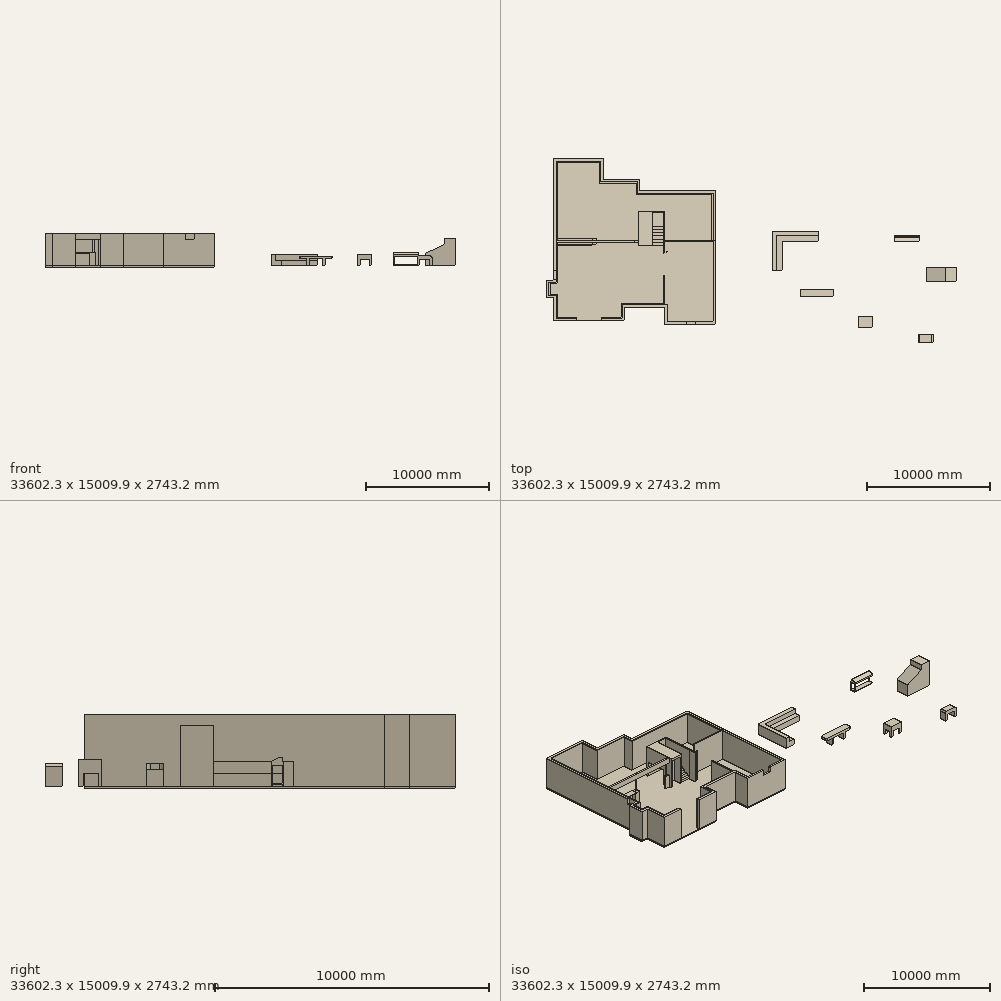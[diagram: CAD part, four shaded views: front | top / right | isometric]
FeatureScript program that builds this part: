
annotation { "Feature Type Name" : "Feature", "Feature Type Description" : "" }
export const myFeature = defineFeature(function(context is Context, id is Id, definition is map)
    precondition{}
    {
        {
            var Q0;
            Q0=qCreatedBy(makeId("Top.planeOp"),FACE);
            var sketch = newSketch(context, id + "F0", { "sketchPlane" : qUnion([Q0])});
            skLineSegment(sketch, "E0", {"start": v(-127, 1524) * mm, "end": v(6096, 1524) * mm});
            skLineSegment(sketch, "E1", {"start": v(6096, 1524) * mm, "end": v(6096, -9042.4) * mm});
            skLineSegment(sketch, "E2", {"start": v(-127, 1524) * mm, "end": v(-127, 2438.4) * mm});
            skLineSegment(sketch, "E3", {"start": v(-127, 2438.4) * mm, "end": v(-3124.2, 2438.4) * mm});
            skLineSegment(sketch, "E4", {"start": v(-3124.2, 2438.4) * mm, "end": v(-3124.2, 4114.8) * mm});
            skLineSegment(sketch, "E5", {"start": v(-3124.2, 4114.8) * mm, "end": v(-6756.4, 4114.8) * mm});
            skLineSegment(sketch, "E6", {"start": v(-6756.4, 4114.8) * mm, "end": v(-6756.4, -5816.6) * mm});
            skLineSegment(sketch, "E7", {"start": v(-6756.4, -5816.6) * mm, "end": v(-7366, -5816.6) * mm});
            skLineSegment(sketch, "E8", {"start": v(-7366, -5816.6) * mm, "end": v(-7366, -6858) * mm});
            skLineSegment(sketch, "E9", {"start": v(-7366, -6858) * mm, "end": v(-6756.4, -6858) * mm});
            skLineSegment(sketch, "E10", {"start": v(-6756.4, -6858) * mm, "end": v(-6756.4, -8737.6) * mm});
            skLineSegment(sketch, "E11", {"start": v(-6756.4, -8737.6) * mm, "end": v(-5080, -8737.6) * mm});
            skLineSegment(sketch, "E12", {"start": v(-5080, -8737.6) * mm, "end": v(-5080, -8890) * mm});
            skLineSegment(sketch, "E13", {"start": v(-3048, -8890) * mm, "end": v(-3048, -8737.6) * mm});
            skLineSegment(sketch, "E14", {"start": v(-3048, -8737.6) * mm, "end": v(-1346.2, -8737.6) * mm});
            skLineSegment(sketch, "E15", {"start": v(-1346.2, -8737.6) * mm, "end": v(-1346.2, -7620) * mm});
            skLineSegment(sketch, "E16", {"start": v(-1346.2, -7620) * mm, "end": v(2311.4, -7620) * mm});
            skLineSegment(sketch, "E17", {"start": v(2311.4, -7620) * mm, "end": v(2311.4, -9042.4) * mm});
            skLineSegment(sketch, "E18", {"start": v(2311.4, -9042.4) * mm, "end": v(6096, -9042.4) * mm});
            skLineSegment(sketch, "E19.bottom", {"start": v(0, 0) * mm, "end": v(2133.6, 0) * mm});
            skLineSegment(sketch, "E19.top", {"start": v(0, -2794) * mm, "end": v(2133.6, -2794) * mm});
            skLineSegment(sketch, "E19.left", {"start": v(0, 0) * mm, "end": v(0, -2794) * mm});
            skLineSegment(sketch, "E19.right", {"start": v(2133.6, 0) * mm, "end": v(2133.6, -2794) * mm});
            skLineSegment(sketch, "E20", {"start": v(2133.6, -2438.4) * mm, "end": v(6096, -2438.4) * mm, "construction": true});
            skLineSegment(sketch, "E21.0", {"start": v(-6959.6, 4318) * mm, "end": v(-6959.6, -5613.4) * mm});
            skLineSegment(sketch, "E21.1", {"start": v(-2921, 4318) * mm, "end": v(-6959.6, 4318) * mm});
            skLineSegment(sketch, "E21.2", {"start": v(76.2, 1727.2) * mm, "end": v(6299.2, 1727.2) * mm});
            skLineSegment(sketch, "E21.3", {"start": v(76.2, 1727.2) * mm, "end": v(76.2, 2641.6) * mm});
            skLineSegment(sketch, "E21.4", {"start": v(76.2, 2641.6) * mm, "end": v(-2921, 2641.6) * mm});
            skLineSegment(sketch, "E21.5", {"start": v(-2921, 2641.6) * mm, "end": v(-2921, 4318) * mm});
            skLineSegment(sketch, "E22.0", {"start": v(-6959.6, -8940.8) * mm, "end": v(-5080, -8940.8) * mm});
            skLineSegment(sketch, "E22.1", {"start": v(-6959.6, -5613.4) * mm, "end": v(-7569.2, -5613.4) * mm});
            skLineSegment(sketch, "E22.2", {"start": v(-7569.2, -5613.4) * mm, "end": v(-7569.2, -7061.2) * mm});
            skLineSegment(sketch, "E22.3", {"start": v(-7569.2, -7061.2) * mm, "end": v(-6959.6, -7061.2) * mm});
            skLineSegment(sketch, "E22.4", {"start": v(-6959.6, -7061.2) * mm, "end": v(-6959.6, -8940.8) * mm});
            skLineSegment(sketch, "E23.0", {"start": v(-3048, -8940.8) * mm, "end": v(-1143, -8940.8) * mm});
            skLineSegment(sketch, "E23.1", {"start": v(-1143, -8940.8) * mm, "end": v(-1143, -7823.2) * mm});
            skLineSegment(sketch, "E23.2", {"start": v(6299.2, 1727.2) * mm, "end": v(6299.2, -9245.6) * mm});
            skLineSegment(sketch, "E23.3", {"start": v(2108.2, -9245.6) * mm, "end": v(6299.2, -9245.6) * mm});
            skLineSegment(sketch, "E23.4", {"start": v(2108.2, -7823.2) * mm, "end": v(2108.2, -9245.6) * mm});
            skLineSegment(sketch, "E23.5", {"start": v(-1143, -7823.2) * mm, "end": v(2108.2, -7823.2) * mm});
            skLineSegment(sketch, "E24", {"start": v(-5080, -8940.8) * mm, "end": v(-5080, -8890) * mm});
            skLineSegment(sketch, "E25", {"start": v(-3048, -8940.8) * mm, "end": v(-3048, -8890) * mm});
            skSolve(sketch);
        }
        {
            var Q0;
            Q0=qCreatedBy(makeId("Top.planeOp"),FACE);
            var sketch = newSketch(context, id + "F1", { "sketchPlane" : qUnion([Q0])});
            skCircle(sketch, "E26", {"center": v(-279.4, -2438.4) * mm, "radius": 50.8 * mm});
            skCircle(sketch, "E27", {"center": v(-3632.2, -2438.4) * mm, "radius": 50.8 * mm});
            skCircle(sketch, "E28", {"center": v(2311.4, -3327.4) * mm, "radius": 50.8 * mm});
            skLineSegment(sketch, "E29", {"start": v(-279.4, -2438.4) * mm, "end": v(-3632.2, -2438.4) * mm, "construction": true});
            skSolve(sketch);
        }
        {
            var Q0;
            Q0 = qSketchRegion(id + "F0", true);
            extrude(context, id + "F2", {"entities" : qUnion([Q0]), "depth" : 2641.6 * mm, "offsetDistance" : 25.4 * mm});
        }
        {
            var Q0;
            Q0 = qSketchRegion(id + "F1", true);
            extrude(context, id + "F3", {"entities" : qUnion([Q0]), "depth" : 2641.6 * mm, "offsetDistance" : 25.4 * mm});
        }
        {
            var Q0;
            Q0=qCreatedBy(makeId("Top.planeOp"),FACE);
            var sketch = newSketch(context, id + "F4", { "sketchPlane" : qUnion([Q0])});
            skLineSegment(sketch, "E30", {"start": v(2136.14, -2436.63) * mm, "end": v(6098.54, -2436.63) * mm, "construction": true});
            skLineSegment(sketch, "E31.0", {"start": v(-6957.06, 4319.77) * mm, "end": v(-6957.06, -5611.63) * mm});
            skLineSegment(sketch, "E31.1", {"start": v(-2918.46, 4319.77) * mm, "end": v(-6957.06, 4319.77) * mm});
            skLineSegment(sketch, "E31.2", {"start": v(78.74, 1728.97) * mm, "end": v(6301.74, 1728.97) * mm});
            skLineSegment(sketch, "E31.3", {"start": v(78.74, 1728.97) * mm, "end": v(78.74, 2643.37) * mm});
            skLineSegment(sketch, "E31.4", {"start": v(78.74, 2643.37) * mm, "end": v(-2918.46, 2643.37) * mm});
            skLineSegment(sketch, "E31.5", {"start": v(-2918.46, 2643.37) * mm, "end": v(-2918.46, 4319.77) * mm});
            skLineSegment(sketch, "E32.0", {"start": v(-6957.06, -8939.03) * mm, "end": v(-5077.46, -8939.03) * mm});
            skLineSegment(sketch, "E32.1", {"start": v(-6957.06, -5611.63) * mm, "end": v(-7566.66, -5611.63) * mm});
            skLineSegment(sketch, "E32.2", {"start": v(-7566.66, -5611.63) * mm, "end": v(-7566.66, -7059.43) * mm});
            skLineSegment(sketch, "E32.3", {"start": v(-7566.66, -7059.43) * mm, "end": v(-6957.06, -7059.43) * mm});
            skLineSegment(sketch, "E32.4", {"start": v(-6957.06, -7059.43) * mm, "end": v(-6957.06, -8939.03) * mm});
            skLineSegment(sketch, "E33.0", {"start": v(-3045.46, -8939.03) * mm, "end": v(-1140.46, -8939.03) * mm});
            skLineSegment(sketch, "E33.1", {"start": v(-1140.46, -8939.03) * mm, "end": v(-1140.46, -7821.43) * mm});
            skLineSegment(sketch, "E33.2", {"start": v(6301.74, 1728.97) * mm, "end": v(6301.74, -9243.83) * mm});
            skLineSegment(sketch, "E33.3", {"start": v(2110.74, -9243.83) * mm, "end": v(6301.74, -9243.83) * mm});
            skLineSegment(sketch, "E33.4", {"start": v(2110.74, -7821.43) * mm, "end": v(2110.74, -9243.83) * mm});
            skLineSegment(sketch, "E33.5", {"start": v(-1140.46, -7821.43) * mm, "end": v(2110.74, -7821.43) * mm});
            skLineSegment(sketch, "E34", {"start": v(-5077.46, -8939.03) * mm, "end": v(-3045.46, -8939.03) * mm});
            skSolve(sketch);
        }
        {
            var Q0;
            Q0 = qSketchRegion(id + "F4", true);
            extrude(context, id + "F5", {"entities" : qUnion([Q0]), "oppositeDirection" : true, "depth" : 101.6 * mm, "offsetDistance" : 25.4 * mm});
        }
        {
            var Q0;
            Q0=makeQuery(id+"F2.opExtrude","CAP_FACE",FACE,{"disambiguationData":[OSD([sQuery(id+"F0.wireOp",EDGE,"E0"),sQuery(id+"F0.wireOp",EDGE,"E1"),sQuery(id+"F0.wireOp",EDGE,"E2"),sQuery(id+"F0.wireOp",EDGE,"E3"),sQuery(id+"F0.wireOp",EDGE,"E4"),sQuery(id+"F0.wireOp",EDGE,"E5"),sQuery(id+"F0.wireOp",EDGE,"E6"),sQuery(id+"F0.wireOp",EDGE,"E7"),sQuery(id+"F0.wireOp",EDGE,"E8"),sQuery(id+"F0.wireOp",EDGE,"E9"),sQuery(id+"F0.wireOp",EDGE,"E10"),sQuery(id+"F0.wireOp",EDGE,"E11"),sQuery(id+"F0.wireOp",EDGE,"E12"),sQuery(id+"F0.wireOp",EDGE,"E13"),sQuery(id+"F0.wireOp",EDGE,"E14"),sQuery(id+"F0.wireOp",EDGE,"E15"),sQuery(id+"F0.wireOp",EDGE,"E16"),sQuery(id+"F0.wireOp",EDGE,"E17"),sQuery(id+"F0.wireOp",EDGE,"E18"),sQuery(id+"F0.wireOp",EDGE,"E21.0"),sQuery(id+"F0.wireOp",EDGE,"E21.1"),sQuery(id+"F0.wireOp",EDGE,"E21.2"),sQuery(id+"F0.wireOp",EDGE,"E21.3"),sQuery(id+"F0.wireOp",EDGE,"E21.4"),sQuery(id+"F0.wireOp",EDGE,"E21.5"),sQuery(id+"F0.wireOp",EDGE,"E22.0"),sQuery(id+"F0.wireOp",EDGE,"E22.1"),sQuery(id+"F0.wireOp",EDGE,"E22.2"),sQuery(id+"F0.wireOp",EDGE,"E22.3"),sQuery(id+"F0.wireOp",EDGE,"E22.4"),sQuery(id+"F0.wireOp",EDGE,"E23.0"),sQuery(id+"F0.wireOp",EDGE,"E23.1"),sQuery(id+"F0.wireOp",EDGE,"E23.2"),sQuery(id+"F0.wireOp",EDGE,"E23.3"),sQuery(id+"F0.wireOp",EDGE,"E23.4"),sQuery(id+"F0.wireOp",EDGE,"E23.5"),sQuery(id+"F0.wireOp",EDGE,"E24"),sQuery(id+"F0.wireOp",EDGE,"E25")])],"isStart":false});
            var sketch = newSketch(context, id + "F6", { "sketchPlane" : qUnion([Q0])});
            skLineSegment(sketch, "E35", {"start": v(-6959.6, -5588) * mm, "end": v(-6756.4, -5588) * mm});
            skLineSegment(sketch, "E36", {"start": v(-6756.4, -5588) * mm, "end": v(-6756.4, -4826) * mm});
            skLineSegment(sketch, "E37", {"start": v(-6756.4, -4826) * mm, "end": v(-6959.6, -4826) * mm});
            skLineSegment(sketch, "E38", {"start": v(-6959.6, -4826) * mm, "end": v(-6959.6, -5588) * mm});
            skLineSegment(sketch, "E39.bottom", {"start": v(3886.2, -9245.6) * mm, "end": v(4648.2, -9245.6) * mm});
            skLineSegment(sketch, "E39.top", {"start": v(3886.2, -9042.4) * mm, "end": v(4648.2, -9042.4) * mm});
            skLineSegment(sketch, "E39.left", {"start": v(3886.2, -9245.6) * mm, "end": v(3886.2, -9042.4) * mm});
            skLineSegment(sketch, "E39.right", {"start": v(4648.2, -9245.6) * mm, "end": v(4648.2, -9042.4) * mm});
            skSolve(sketch);
        }
        {
            var Q0;
            Q0 = qSketchRegion(id + "F6", true);
            extrude(context, id + "F7", {"entities" : qUnion([Q0]), "operationType" : NewBodyOperationType.REMOVE, "oppositeDirection" : true, "depth" : 457.2 * mm, "offsetDistance" : 25.4 * mm});
        }
        {
            var Q0;
            Q0=makeQuery(id+"F2.opExtrude","SWEPT_FACE",FACE,{"disambiguationData":[OSD([sQuery(id+"F0.wireOp",EDGE,"E19.top")])]});
            var sketch = newSketch(context, id + "F8", { "sketchPlane" : qUnion([Q0])});
            skLineSegment(sketch, "E40.bottom", {"start": v(1117.6, 0) * mm, "end": v(2032, 0) * mm});
            skLineSegment(sketch, "E40.top", {"start": v(1117.6, 2641.6) * mm, "end": v(2032, 2641.6) * mm});
            skLineSegment(sketch, "E40.left", {"start": v(1117.6, 0) * mm, "end": v(1117.6, 2641.6) * mm});
            skLineSegment(sketch, "E40.right", {"start": v(2032, 0) * mm, "end": v(2032, 2641.6) * mm});
            skSolve(sketch);
        }
        {
            var Q0;
            Q0=makeQuery(id+"F8.imprint","IMPRINT",FACE,{"disambiguationData":[TD([[makeQuery(id+"F8.imprint","IMPRINT",EDGE,{"derivedFrom":sQuery(id+"F8.wireOp",EDGE,"E40.bottom")}),1.0]])]});
            extrude(context, id + "F9", {"entities" : qUnion([Q0]), "operationType" : NewBodyOperationType.REMOVE, "oppositeDirection" : true, "depth" : 2692.4 * mm, "offsetDistance" : 25.4 * mm});
        }
        {
            var Q0;
            Q0=makeQuery(id+"F2.opExtrude","SWEPT_FACE",FACE,{"disambiguationData":[OSD([sQuery(id+"F0.wireOp",EDGE,"E19.right")])]});
            var sketch = newSketch(context, id + "F10", { "sketchPlane" : qUnion([Q0])});
            skLineSegment(sketch, "E41", {"start": v(-2755.4, 0) * mm, "end": v(-2755.4, 203.2) * mm});
            skLineSegment(sketch, "E42", {"start": v(-2755.4, 203.2) * mm, "end": v(-2501.4, 203.2) * mm});
            skLineSegment(sketch, "E43", {"start": v(-2501.4, 203.2) * mm, "end": v(-2501.4, 406.4) * mm});
            skLineSegment(sketch, "E44", {"start": v(-2501.4, 406.4) * mm, "end": v(-2247.4, 406.4) * mm});
            skLineSegment(sketch, "E45", {"start": v(-2247.4, 406.4) * mm, "end": v(-2247.4, 609.6) * mm});
            skLineSegment(sketch, "E46", {"start": v(-2247.4, 609.6) * mm, "end": v(-1993.4, 609.6) * mm});
            skLineSegment(sketch, "E47", {"start": v(-1993.4, 609.6) * mm, "end": v(-1993.4, 812.8) * mm});
            skLineSegment(sketch, "E48", {"start": v(-1993.4, 812.8) * mm, "end": v(-1739.4, 812.8) * mm});
            skLineSegment(sketch, "E49", {"start": v(-1739.4, 812.8) * mm, "end": v(-1739.4, 1016) * mm});
            skLineSegment(sketch, "E50", {"start": v(-1739.4, 1016) * mm, "end": v(-1485.4, 1016) * mm});
            skLineSegment(sketch, "E51", {"start": v(0, 1121.03) * mm, "end": v(0, 0) * mm});
            skLineSegment(sketch, "E52", {"start": v(0, 0) * mm, "end": v(-2755.4, 0) * mm});
            skLineSegment(sketch, "E53", {"start": v(-1485.4, 1016) * mm, "end": v(-1485.4, 1219.2) * mm});
            skLineSegment(sketch, "E54", {"start": v(-1485.4, 1219.2) * mm, "end": v(-1231.4, 1219.2) * mm});
            skLineSegment(sketch, "E55", {"start": v(-1231.4, 1219.2) * mm, "end": v(-1231.4, 1422.4) * mm});
            skLineSegment(sketch, "E56", {"start": v(-1231.4, 1422.4) * mm, "end": v(0, 1422.4) * mm});
            skLineSegment(sketch, "E57", {"start": v(0, 1422.4) * mm, "end": v(0, 1121.03) * mm});
            skSolve(sketch);
        }
        {
            var Q0;
            Q0=makeQuery(id+"F10.imprint","IMPRINT",FACE,{"disambiguationData":[TD([[makeQuery(id+"F10.imprint","IMPRINT",EDGE,{"derivedFrom":sQuery(id+"F10.wireOp",EDGE,"E41")}),-1.0]])]});
            extrude(context, id + "F11", {"entities" : qUnion([Q0]), "operationType" : NewBodyOperationType.ADD, "oppositeDirection" : true, "depth" : 1016 * mm, "offsetDistance" : 25.4 * mm});
        }
        {
            var Q0;
            Q0=makeQuery(id+"F5.opExtrude","CAP_FACE",FACE,{"disambiguationData":[OSD([sQuery(id+"F4.wireOp",EDGE,"E31.0"),sQuery(id+"F4.wireOp",EDGE,"E31.1"),sQuery(id+"F4.wireOp",EDGE,"E31.2"),sQuery(id+"F4.wireOp",EDGE,"E31.3"),sQuery(id+"F4.wireOp",EDGE,"E31.4"),sQuery(id+"F4.wireOp",EDGE,"E31.5"),sQuery(id+"F4.wireOp",EDGE,"E32.0"),sQuery(id+"F4.wireOp",EDGE,"E32.1"),sQuery(id+"F4.wireOp",EDGE,"E32.2"),sQuery(id+"F4.wireOp",EDGE,"E32.3"),sQuery(id+"F4.wireOp",EDGE,"E32.4"),sQuery(id+"F4.wireOp",EDGE,"E33.0"),sQuery(id+"F4.wireOp",EDGE,"E33.1"),sQuery(id+"F4.wireOp",EDGE,"E33.2"),sQuery(id+"F4.wireOp",EDGE,"E33.3"),sQuery(id+"F4.wireOp",EDGE,"E33.4"),sQuery(id+"F4.wireOp",EDGE,"E33.5"),sQuery(id+"F4.wireOp",EDGE,"E34")])],"isStart":true});
            var sketch = newSketch(context, id + "F12", { "sketchPlane" : qUnion([Q0])});
            skLineSegment(sketch, "E58.bottom", {"start": v(2133.6, -2438.4) * mm, "end": v(6197.6, -2438.4) * mm});
            skLineSegment(sketch, "E58.top", {"start": v(2133.6, -2336.8) * mm, "end": v(6197.6, -2336.8) * mm});
            skLineSegment(sketch, "E58.left", {"start": v(2133.6, -2438.4) * mm, "end": v(2133.6, -2336.8) * mm});
            skLineSegment(sketch, "E58.right", {"start": v(6197.6, -2438.4) * mm, "end": v(6197.6, -2336.8) * mm});
            skSolve(sketch);
        }
        {
            var Q0;
            Q0 = qSketchRegion(id + "F12", true);
            extrude(context, id + "F13", {"entities" : qUnion([Q0]), "depth" : 2641.6 * mm, "offsetDistance" : 25.4 * mm});
        }
        {
            var Q0;
            Q0=makeQuery(id+"F5.opExtrude","CAP_FACE",FACE,{"disambiguationData":[OSD([sQuery(id+"F4.wireOp",EDGE,"E31.0"),sQuery(id+"F4.wireOp",EDGE,"E31.1"),sQuery(id+"F4.wireOp",EDGE,"E31.2"),sQuery(id+"F4.wireOp",EDGE,"E31.3"),sQuery(id+"F4.wireOp",EDGE,"E31.4"),sQuery(id+"F4.wireOp",EDGE,"E31.5"),sQuery(id+"F4.wireOp",EDGE,"E32.0"),sQuery(id+"F4.wireOp",EDGE,"E32.1"),sQuery(id+"F4.wireOp",EDGE,"E32.2"),sQuery(id+"F4.wireOp",EDGE,"E32.3"),sQuery(id+"F4.wireOp",EDGE,"E32.4"),sQuery(id+"F4.wireOp",EDGE,"E33.0"),sQuery(id+"F4.wireOp",EDGE,"E33.1"),sQuery(id+"F4.wireOp",EDGE,"E33.2"),sQuery(id+"F4.wireOp",EDGE,"E33.3"),sQuery(id+"F4.wireOp",EDGE,"E33.4"),sQuery(id+"F4.wireOp",EDGE,"E33.5"),sQuery(id+"F4.wireOp",EDGE,"E34")])],"isStart":true});
            var sketch = newSketch(context, id + "F14", { "sketchPlane" : qUnion([Q0])});
            skLineSegment(sketch, "E59.bottom", {"start": v(2032, -2794) * mm, "end": v(2133.6, -2794) * mm});
            skLineSegment(sketch, "E59.top", {"start": v(2032, -3403.6) * mm, "end": v(2133.6, -3403.6) * mm});
            skLineSegment(sketch, "E59.left", {"start": v(2032, -2794) * mm, "end": v(2032, -3403.6) * mm});
            skLineSegment(sketch, "E59.right", {"start": v(2133.6, -2794) * mm, "end": v(2133.6, -3403.6) * mm});
            skLineSegment(sketch, "E60", {"start": v(2133.6, -3403.6) * mm, "end": v(2133.6, -5232.4) * mm, "construction": true});
            skLineSegment(sketch, "E61.bottom", {"start": v(2133.6, -5232.4) * mm, "end": v(2032, -5232.4) * mm});
            skLineSegment(sketch, "E61.top", {"start": v(2133.6, -7649.03) * mm, "end": v(2032, -7649.03) * mm});
            skLineSegment(sketch, "E61.left", {"start": v(2133.6, -5232.4) * mm, "end": v(2133.6, -7649.03) * mm});
            skLineSegment(sketch, "E61.right", {"start": v(2032, -5232.4) * mm, "end": v(2032, -7649.03) * mm});
            skSolve(sketch);
        }
        {
            var Q0;
            Q0 = qSketchRegion(id + "F14", true);
            extrude(context, id + "F15", {"entities" : qUnion([Q0]), "depth" : 2641.6 * mm, "offsetDistance" : 25.4 * mm});
        }
        {
            var Q0;
            Q0=makeQuery(id+"F5.opExtrude","CAP_FACE",FACE,{"disambiguationData":[OSD([sQuery(id+"F4.wireOp",EDGE,"E31.0"),sQuery(id+"F4.wireOp",EDGE,"E31.1"),sQuery(id+"F4.wireOp",EDGE,"E31.2"),sQuery(id+"F4.wireOp",EDGE,"E31.3"),sQuery(id+"F4.wireOp",EDGE,"E31.4"),sQuery(id+"F4.wireOp",EDGE,"E31.5"),sQuery(id+"F4.wireOp",EDGE,"E32.0"),sQuery(id+"F4.wireOp",EDGE,"E32.1"),sQuery(id+"F4.wireOp",EDGE,"E32.2"),sQuery(id+"F4.wireOp",EDGE,"E32.3"),sQuery(id+"F4.wireOp",EDGE,"E32.4"),sQuery(id+"F4.wireOp",EDGE,"E33.0"),sQuery(id+"F4.wireOp",EDGE,"E33.1"),sQuery(id+"F4.wireOp",EDGE,"E33.2"),sQuery(id+"F4.wireOp",EDGE,"E33.3"),sQuery(id+"F4.wireOp",EDGE,"E33.4"),sQuery(id+"F4.wireOp",EDGE,"E33.5"),sQuery(id+"F4.wireOp",EDGE,"E34")])],"isStart":true});
            var sketch = newSketch(context, id + "F16", { "sketchPlane" : qUnion([Q0])});
            skLineSegment(sketch, "E62.bottom", {"start": v(-6654.8, -2667) * mm, "end": v(-3479.8, -2667) * mm});
            skLineSegment(sketch, "E62.top", {"start": v(-6654.8, -2209.8) * mm, "end": v(-3479.8, -2209.8) * mm});
            skLineSegment(sketch, "E62.left", {"start": v(-6654.8, -2667) * mm, "end": v(-6654.8, -2209.8) * mm});
            skLineSegment(sketch, "E62.right", {"start": v(-3479.8, -2667) * mm, "end": v(-3479.8, -2209.8) * mm});
            skLineSegment(sketch, "E63.bottom", {"start": v(0, -2540) * mm, "end": v(-406.4, -2540) * mm});
            skLineSegment(sketch, "E63.top", {"start": v(0, -2349.5) * mm, "end": v(-406.4, -2349.5) * mm});
            skLineSegment(sketch, "E63.left", {"start": v(0, -2540) * mm, "end": v(0, -2349.5) * mm});
            skLineSegment(sketch, "E63.right", {"start": v(-406.4, -2540) * mm, "end": v(-406.4, -2349.5) * mm});
            skSolve(sketch);
        }
        {
            var Q0;
            Q0 = qSketchRegion(id + "F16", true);
            extrude(context, id + "F17", {"entities" : qUnion([Q0]), "depth" : 1066.8 * mm, "offsetDistance" : 25.4 * mm});
        }
        {
            var Q0;
            {var subQ0=sQuery(id+"F0.wireOp",EDGE,"E18");var subQ1=sQuery(id+"F0.wireOp",EDGE,"E6");var subQ2=sQuery(id+"F0.wireOp",EDGE,"E21.4");var subQ3=sQuery(id+"F0.wireOp",EDGE,"E5");var subQ4=sQuery(id+"F0.wireOp",EDGE,"E21.3");var subQ5=sQuery(id+"F0.wireOp",EDGE,"E21.1");var subQ6=sQuery(id+"F0.wireOp",EDGE,"E3");var subQ7=sQuery(id+"F0.wireOp",EDGE,"E4");var subQ8=sQuery(id+"F0.wireOp",EDGE,"E21.2");var subQ9=sQuery(id+"F0.wireOp",EDGE,"E0");var subQ10=sQuery(id+"F0.wireOp",EDGE,"E21.0");var subQ11=sQuery(id+"F0.wireOp",EDGE,"E2");var subQ12=sQuery(id+"F0.wireOp",EDGE,"E1");var subQ13=sQuery(id+"F0.wireOp",EDGE,"E21.5");var subQ14=sQuery(id+"F0.wireOp",EDGE,"E23.2");var subQ15=sQuery(id+"F0.wireOp",EDGE,"E23.3");Q0=makeQuery(id+"F7.boolean.opBoolean","SPLIT",FACE,{"disambiguationData":[TD([makeQuery(id+"F2.opExtrude","SWEPT_FACE",FACE,{"disambiguationData":[OSD([subQ9])]})])],"derivedFrom":makeQuery(id+"F2.opExtrude","CAP_FACE",FACE,{"disambiguationData":[OSD([subQ9,subQ12,subQ11,subQ6,subQ7,subQ3,subQ1,sQuery(id+"F0.wireOp",EDGE,"E7"),sQuery(id+"F0.wireOp",EDGE,"E8"),sQuery(id+"F0.wireOp",EDGE,"E9"),sQuery(id+"F0.wireOp",EDGE,"E10"),sQuery(id+"F0.wireOp",EDGE,"E11"),sQuery(id+"F0.wireOp",EDGE,"E12"),sQuery(id+"F0.wireOp",EDGE,"E13"),sQuery(id+"F0.wireOp",EDGE,"E14"),sQuery(id+"F0.wireOp",EDGE,"E15"),sQuery(id+"F0.wireOp",EDGE,"E16"),sQuery(id+"F0.wireOp",EDGE,"E17"),subQ0,subQ10,subQ5,subQ8,subQ4,subQ2,subQ13,sQuery(id+"F0.wireOp",EDGE,"E22.0"),sQuery(id+"F0.wireOp",EDGE,"E22.1"),sQuery(id+"F0.wireOp",EDGE,"E22.2"),sQuery(id+"F0.wireOp",EDGE,"E22.3"),sQuery(id+"F0.wireOp",EDGE,"E22.4"),sQuery(id+"F0.wireOp",EDGE,"E23.0"),sQuery(id+"F0.wireOp",EDGE,"E23.1"),subQ14,subQ15,sQuery(id+"F0.wireOp",EDGE,"E23.4"),sQuery(id+"F0.wireOp",EDGE,"E23.5"),sQuery(id+"F0.wireOp",EDGE,"E24"),sQuery(id+"F0.wireOp",EDGE,"E25")])],"isStart":false})});}
            var sketch = newSketch(context, id + "F18", { "sketchPlane" : qUnion([Q0])});
            skLineSegment(sketch, "E64.bottom", {"start": v(0, -2349.5) * mm, "end": v(-6756.4, -2349.5) * mm});
            skLineSegment(sketch, "E64.top", {"start": v(0, -2540.11) * mm, "end": v(-6756.4, -2540.11) * mm});
            skLineSegment(sketch, "E64.left", {"start": v(0, -2349.5) * mm, "end": v(0, -2540.11) * mm});
            skLineSegment(sketch, "E64.right", {"start": v(-6756.4, -2349.5) * mm, "end": v(-6756.4, -2540.11) * mm});
            skSolve(sketch);
        }
        {
            var Q0;
            Q0 = qSketchRegion(id + "F18", true);
            extrude(context, id + "F19", {"entities" : qUnion([Q0]), "oppositeDirection" : true, "depth" : 457.2 * mm, "offsetDistance" : 25.4 * mm});
        }
        {
            var Q0;
            Q0=makeQuery(id+"F5.opExtrude","CAP_FACE",FACE,{"disambiguationData":[OSD([sQuery(id+"F4.wireOp",EDGE,"E31.0"),sQuery(id+"F4.wireOp",EDGE,"E31.1"),sQuery(id+"F4.wireOp",EDGE,"E31.2"),sQuery(id+"F4.wireOp",EDGE,"E31.3"),sQuery(id+"F4.wireOp",EDGE,"E31.4"),sQuery(id+"F4.wireOp",EDGE,"E31.5"),sQuery(id+"F4.wireOp",EDGE,"E32.0"),sQuery(id+"F4.wireOp",EDGE,"E32.1"),sQuery(id+"F4.wireOp",EDGE,"E32.2"),sQuery(id+"F4.wireOp",EDGE,"E32.3"),sQuery(id+"F4.wireOp",EDGE,"E32.4"),sQuery(id+"F4.wireOp",EDGE,"E33.0"),sQuery(id+"F4.wireOp",EDGE,"E33.1"),sQuery(id+"F4.wireOp",EDGE,"E33.2"),sQuery(id+"F4.wireOp",EDGE,"E33.3"),sQuery(id+"F4.wireOp",EDGE,"E33.4"),sQuery(id+"F4.wireOp",EDGE,"E33.5"),sQuery(id+"F4.wireOp",EDGE,"E34")])],"isStart":true});
            var sketch = newSketch(context, id + "F20", { "sketchPlane" : qUnion([Q0])});
            skLineSegment(sketch, "E65.0", {"start": v(-6654.8, -8636) * mm, "end": v(-5080, -8636) * mm});
            skLineSegment(sketch, "E65.1", {"start": v(-6654.8, -6756.4) * mm, "end": v(-6654.8, -8636) * mm});
            skLineSegment(sketch, "E65.2", {"start": v(-228.6, 2336.8) * mm, "end": v(-3225.8, 2336.8) * mm});
            skLineSegment(sketch, "E65.3", {"start": v(-228.6, 1422.4) * mm, "end": v(-228.6, 2336.8) * mm});
            skLineSegment(sketch, "E65.4", {"start": v(-228.6, 1422.4) * mm, "end": v(5994.4, 1422.4) * mm});
            skLineSegment(sketch, "E65.5", {"start": v(5994.4, 1422.4) * mm, "end": v(5994.4, -2379.6) * mm});
            skLineSegment(sketch, "E65.6", {"start": v(-3225.8, 2336.8) * mm, "end": v(-3225.8, 4013.2) * mm});
            skLineSegment(sketch, "E65.7", {"start": v(-3225.8, 4013.2) * mm, "end": v(-6654.8, 4013.2) * mm});
            skLineSegment(sketch, "E65.8", {"start": v(-6654.8, 4013.2) * mm, "end": v(-6654.8, -5918.2) * mm});
            skLineSegment(sketch, "E65.9", {"start": v(-6654.8, -5918.2) * mm, "end": v(-7264.4, -5918.2) * mm});
            skLineSegment(sketch, "E65.10", {"start": v(-7264.4, -5918.2) * mm, "end": v(-7264.4, -6756.4) * mm});
            skLineSegment(sketch, "E65.11", {"start": v(-7264.4, -6756.4) * mm, "end": v(-6654.8, -6756.4) * mm});
            skPoint(sketch, "E66", {"position": v(5994.4, -2379.6) * mm});
            skLineSegment(sketch, "E67", {"start": v(5994.4, -2379.6) * mm, "end": v(6096, -2379.6) * mm});
            skLineSegment(sketch, "E68.0.0", {"start": v(4648.2, -9042.4) * mm, "end": v(4648.2, -9245.6) * mm});
            skLineSegment(sketch, "E68.0.1", {"start": v(4648.2, -9245.6) * mm, "end": v(6299.2, -9245.6) * mm});
            skLineSegment(sketch, "E68.0.10", {"start": v(-6756.4, -4826) * mm, "end": v(-6756.4, 4114.8) * mm});
            skLineSegment(sketch, "E68.0.11", {"start": v(-6756.4, 4114.8) * mm, "end": v(-3124.2, 4114.8) * mm});
            skLineSegment(sketch, "E68.0.12", {"start": v(-3124.2, 4114.8) * mm, "end": v(-3124.2, 2438.4) * mm});
            skLineSegment(sketch, "E68.0.13", {"start": v(-3124.2, 2438.4) * mm, "end": v(-127, 2438.4) * mm});
            skLineSegment(sketch, "E68.0.14", {"start": v(-127, 2438.4) * mm, "end": v(-127, 1524) * mm});
            skLineSegment(sketch, "E68.0.15", {"start": v(-127, 1524) * mm, "end": v(6096, 1524) * mm});
            skLineSegment(sketch, "E68.0.16", {"start": v(6096, 1524) * mm, "end": v(6096, -2379.6) * mm});
            skLineSegment(sketch, "E68.0.17", {"start": v(6096, -9042.4) * mm, "end": v(4648.2, -9042.4) * mm});
            skPoint(sketch, "E69.orphan", {"position": v(6096, -9042.4) * mm});
            skPoint(sketch, "E68.0.3.end.orphan", {"position": v(76.2, 1727.2) * mm});
            skPoint(sketch, "E68.0.2.end.orphan", {"position": v(6299.2, 1727.2) * mm});
            skPoint(sketch, "E68.0.5.start.orphan", {"position": v(76.2, 2641.6) * mm});
            skPoint(sketch, "E68.0.6.start.orphan", {"position": v(-2921, 2641.6) * mm});
            skPoint(sketch, "E68.0.7.start.orphan", {"position": v(-2921, 4318) * mm});
            skPoint(sketch, "E68.0.8.start.orphan", {"position": v(-6959.6, 4318) * mm});
            skPoint(sketch, "E68.0.9.start.orphan", {"position": v(-6959.6, -4826) * mm});
            skLineSegment(sketch, "E70.0", {"start": v(-6756.4, -8737.6) * mm, "end": v(-5080, -8737.6) * mm});
            skLineSegment(sketch, "E71.0", {"start": v(-6756.4, -6858) * mm, "end": v(-6756.4, -8737.6) * mm});
            skLineSegment(sketch, "E72.0", {"start": v(-7366, -6858) * mm, "end": v(-6756.4, -6858) * mm});
            skLineSegment(sketch, "E73.0", {"start": v(-7366, -5816.6) * mm, "end": v(-7366, -6858) * mm});
            skLineSegment(sketch, "E74.0", {"start": v(-6756.4, -5816.6) * mm, "end": v(-7366, -5816.6) * mm});
            skLineSegment(sketch, "E75", {"start": v(-5080, -8737.6) * mm, "end": v(-5080, -8636) * mm});
            skLineSegment(sketch, "E76", {"start": v(-6756.4, -5816.6) * mm, "end": v(-6756.4, -4826) * mm});
            skLineSegment(sketch, "E77.0", {"start": v(-1447.8, -7518.4) * mm, "end": v(2102.79, -7518.4) * mm});
            skLineSegment(sketch, "E77.1", {"start": v(-1447.8, -8636) * mm, "end": v(-1447.8, -7518.4) * mm});
            skLineSegment(sketch, "E77.2", {"start": v(-3048, -8636) * mm, "end": v(-1447.8, -8636) * mm});
            skLineSegment(sketch, "E78.0", {"start": v(-3048, -8737.6) * mm, "end": v(-1346.2, -8737.6) * mm});
            skLineSegment(sketch, "E79.0", {"start": v(-1346.2, -8737.6) * mm, "end": v(-1346.2, -7620) * mm});
            skLineSegment(sketch, "E80.0", {"start": v(-1346.2, -7620) * mm, "end": v(2102.79, -7620) * mm});
            skLineSegment(sketch, "E81", {"start": v(-3048, -8737.6) * mm, "end": v(-3048, -8636) * mm});
            skLineSegment(sketch, "E82", {"start": v(2102.79, -7620) * mm, "end": v(2102.79, -7518.4) * mm});
            skPoint(sketch, "E83.orphan", {"position": v(2311.4, -7620) * mm});
            skSolve(sketch);
        }
        {
            var Q0;
            Q0=makeQuery(id+"F20.imprint","IMPRINT",FACE,{"disambiguationData":[TD([[makeQuery(id+"F20.imprint","IMPRINT",EDGE,{"derivedFrom":sQuery(id+"F20.wireOp",EDGE,"E65.0")}),-1.0]])]});
            var Q1;
            Q1=makeQuery(id+"F20.imprint","IMPRINT",FACE,{"disambiguationData":[TD([[makeQuery(id+"F20.imprint","IMPRINT",EDGE,{"derivedFrom":sQuery(id+"F20.wireOp",EDGE,"E77.0")}),-1.0]])]});
            extrude(context, id + "F21", {"entities" : qUnion([Q0, Q1]), "depth" : 2641.6 * mm, "offsetDistance" : 25.4 * mm});
        }
        {
            var Q0;
            {var subQ1=sQuery(id+"F0.wireOp",EDGE,"E19.left");var subQ2=sQuery(id+"F0.wireOp",EDGE,"E19.top");Q0=makeQuery(id+"F9.boolean.opBoolean","SPLIT",FACE,{"disambiguationData":[TD([makeQuery(id+"F2.opExtrude","SWEPT_FACE",FACE,{"disambiguationData":[OSD([subQ1])]})])],"derivedFrom":makeQuery(id+"F2.opExtrude","SWEPT_FACE",FACE,{"disambiguationData":[OSD([subQ2])]})});}
            var sketch = newSketch(context, id + "F22", { "sketchPlane" : qUnion([Q0])});
            skLineSegment(sketch, "E84.bottom", {"start": v(76.2, 0) * mm, "end": v(1028.7, 0) * mm});
            skLineSegment(sketch, "E84.top", {"start": v(76.2, 2438.4) * mm, "end": v(1028.7, 2438.4) * mm});
            skLineSegment(sketch, "E84.left", {"start": v(76.2, 0) * mm, "end": v(76.2, 2438.4) * mm});
            skLineSegment(sketch, "E84.right", {"start": v(1028.7, 0) * mm, "end": v(1028.7, 2438.4) * mm});
            skSolve(sketch);
        }
        {
            var Q0;
            Q0=makeQuery(id+"F22.imprint","IMPRINT",FACE,{"disambiguationData":[TD([[makeQuery(id+"F22.imprint","IMPRINT",EDGE,{"derivedFrom":sQuery(id+"F22.wireOp",EDGE,"E84.bottom")}),1.0]])]});
            extrude(context, id + "F23", {"entities" : qUnion([Q0]), "operationType" : NewBodyOperationType.REMOVE, "oppositeDirection" : true, "depth" : 762 * mm, "offsetDistance" : 25.4 * mm});
        }
        {
            var Q0;
            Q0=makeQuery(id+"F2.opExtrude","SWEPT_FACE",FACE,{"disambiguationData":[OSD([sQuery(id+"F0.wireOp",EDGE,"E19.left")])]});
            var sketch = newSketch(context, id + "F24", { "sketchPlane" : qUnion([Q0])});
            skLineSegment(sketch, "E85.bottom", {"start": v(152.4, 0) * mm, "end": v(1930.4, 0) * mm});
            skLineSegment(sketch, "E85.top", {"start": v(152.4, 1270) * mm, "end": v(1930.4, 1270) * mm});
            skLineSegment(sketch, "E85.left", {"start": v(152.4, 0) * mm, "end": v(152.4, 1270) * mm});
            skLineSegment(sketch, "E85.right", {"start": v(1930.4, 0) * mm, "end": v(1930.4, 1270) * mm});
            skSolve(sketch);
        }
        {
            var Q0;
            Q0=makeQuery(id+"F9.boolean.opBoolean","COPY",FACE,{"derivedFrom":makeQuery(id+"F9.opExtrude","SWEPT_FACE",FACE,{"disambiguationData":[OSD([sQuery(id+"F8.wireOp",EDGE,"E40.left")])]})});
            var Q1;
            Q1=makeQuery(id+"F9.boolean.opBoolean","COPY",FACE,{"derivedFrom":makeQuery(id+"F9.opExtrude","SWEPT_FACE",FACE,{"disambiguationData":[OSD([sQuery(id+"F8.wireOp",EDGE,"E40.right")])]})});
            var Q2;
            Q2=makeQuery(id+"F24.imprint","IMPRINT",FACE,{"disambiguationData":[TD([[makeQuery(id+"F24.imprint","IMPRINT",EDGE,{"derivedFrom":sQuery(id+"F24.wireOp",EDGE,"E85.bottom")}),1.0]])]});
            extrude(context, id + "F25", {"entities" : qUnion([Q0, Q1, Q2]), "operationType" : NewBodyOperationType.REMOVE, "depth" : 914.4 * mm, "offsetDistance" : 25.4 * mm});
        }
        {
            var Q0;
            Q0=makeQuery(id+"F25.boolean.opBoolean","COPY",FACE,{"derivedFrom":makeQuery(id+"F25.opExtrude","CAP_FACE",FACE,{"disambiguationData":[OSD([sQuery(id+"F24.wireOp",EDGE,"E85.bottom"),sQuery(id+"F24.wireOp",EDGE,"E85.top"),sQuery(id+"F24.wireOp",EDGE,"E85.left"),sQuery(id+"F24.wireOp",EDGE,"E85.right")])],"isStart":false})});
            var sketch = newSketch(context, id + "F26", { "sketchPlane" : qUnion([Q0])});
            skLineSegment(sketch, "E86.bottom", {"start": v(152.4, 0) * mm, "end": v(1066.8, 0) * mm});
            skLineSegment(sketch, "E86.top", {"start": v(152.4, 1270) * mm, "end": v(1066.8, 1270) * mm});
            skLineSegment(sketch, "E86.left", {"start": v(152.4, 0) * mm, "end": v(152.4, 1270) * mm});
            skLineSegment(sketch, "E86.right", {"start": v(1066.8, 0) * mm, "end": v(1066.8, 1270) * mm});
            skSolve(sketch);
        }
        {
            var Q0;
            Q0=makeQuery(id+"F26.imprint","IMPRINT",FACE,{"disambiguationData":[TD([[makeQuery(id+"F26.imprint","IMPRINT",EDGE,{"derivedFrom":sQuery(id+"F26.wireOp",EDGE,"E86.bottom")}),1.0]])]});
            extrude(context, id + "F27", {"entities" : qUnion([Q0]), "operationType" : NewBodyOperationType.REMOVE, "oppositeDirection" : true, "depth" : 1219.2 * mm, "offsetDistance" : 25.4 * mm});
        }
        {
            var Q0;
            Q0=makeQuery(id+"F16.imprint","IMPRINT",FACE,{"disambiguationData":[TD([[makeQuery(id+"F16.imprint","IMPRINT",EDGE,{"derivedFrom":sQuery(id+"F16.wireOp",EDGE,"E62.bottom")}),-1.0]])]});
            var sketch = newSketch(context, id + "F28", { "sketchPlane" : qUnion([Q0])});
            skSolve(sketch);
        }
        {
            var Q0;
            Q0=makeQuery(id+"F17.opExtrude","SWEPT_FACE",FACE,{"disambiguationData":[OSD([sQuery(id+"F16.wireOp",EDGE,"E62.bottom")])]});
            var sketch = newSketch(context, id + "F29", { "sketchPlane" : qUnion([Q0])});
            skLineSegment(sketch, "E87.bottom", {"start": v(-6502.4, 0) * mm, "end": v(-3937, 0) * mm});
            skLineSegment(sketch, "E87.top", {"start": v(-6502.4, 990.6) * mm, "end": v(-3937, 990.6) * mm});
            skLineSegment(sketch, "E87.left", {"start": v(-6502.4, 0) * mm, "end": v(-6502.4, 990.6) * mm});
            skLineSegment(sketch, "E87.right", {"start": v(-3937, 0) * mm, "end": v(-3937, 990.6) * mm});
            skSolve(sketch);
        }
        {
            var Q0;
            Q0=makeQuery(id+"F29.imprint","IMPRINT",FACE,{"disambiguationData":[TD([[makeQuery(id+"F29.imprint","IMPRINT",EDGE,{"derivedFrom":sQuery(id+"F29.wireOp",EDGE,"E87.bottom")}),1.0]])]});
            extrude(context, id + "F30", {"entities" : qUnion([Q0]), "operationType" : NewBodyOperationType.REMOVE, "oppositeDirection" : true, "depth" : 304.8 * mm, "offsetDistance" : 25.4 * mm});
        }
        {
            var Q0;
            Q0=makeQuery(id+"F2.opExtrude","SWEPT_FACE",FACE,{"disambiguationData":[OSD([sQuery(id+"F0.wireOp",EDGE,"E19.bottom")])]});
            var sketch = newSketch(context, id + "F31", { "sketchPlane" : qUnion([Q0])});
            skLineSegment(sketch, "E88.bottom", {"start": v(-2133.6, 0) * mm, "end": v(-2032, 0) * mm});
            skLineSegment(sketch, "E88.top", {"start": v(-2133.6, 2641.6) * mm, "end": v(-2032, 2641.6) * mm});
            skLineSegment(sketch, "E88.left", {"start": v(-2133.6, 0) * mm, "end": v(-2133.6, 2641.6) * mm});
            skLineSegment(sketch, "E88.right", {"start": v(-2032, 0) * mm, "end": v(-2032, 2641.6) * mm});
            skSolve(sketch);
        }
        {
            var Q0;
            Q0=makeQuery(id+"F31.imprint","IMPRINT",FACE,{"disambiguationData":[TD([[makeQuery(id+"F31.imprint","IMPRINT",EDGE,{"derivedFrom":sQuery(id+"F31.wireOp",EDGE,"E88.bottom")}),-1.0]])]});
            extrude(context, id + "F32", {"entities" : qUnion([Q0]), "oppositeDirection" : true, "depth" : 2794 * mm, "offsetDistance" : 25.4 * mm});
        }
        {
            var Q0;
            Q0=makeQuery(id+"F32.opExtrude","SWEPT_BODY",BODY,{"disambiguationData":[OSD([sQuery(id+"F31.wireOp",EDGE,"E88.bottom"),sQuery(id+"F31.wireOp",EDGE,"E88.top"),sQuery(id+"F31.wireOp",EDGE,"E88.left"),sQuery(id+"F31.wireOp",EDGE,"E88.right")])]});
            var Q1;
            Q1=makeQuery(id+"F2.opExtrude","SWEPT_BODY",BODY,{"disambiguationData":[OSD([sQuery(id+"F0.wireOp",EDGE,"E19.bottom"),sQuery(id+"F0.wireOp",EDGE,"E19.top"),sQuery(id+"F0.wireOp",EDGE,"E19.left"),sQuery(id+"F0.wireOp",EDGE,"E19.right")])]});
            booleanBodies(context, id + "F33", {"operationType" : BooleanOperationType.UNION, "tools" : qUnion([Q0, Q1])});
        }
        {
            var Q0;
            Q0=makeQuery(id+"F17.opExtrude","CAP_FACE",FACE,{"disambiguationData":[OSD([sQuery(id+"F16.wireOp",EDGE,"E62.bottom"),sQuery(id+"F16.wireOp",EDGE,"E62.top"),sQuery(id+"F16.wireOp",EDGE,"E62.left"),sQuery(id+"F16.wireOp",EDGE,"E62.right")])],"isStart":false});
            var sketch = newSketch(context, id + "F34", { "sketchPlane" : qUnion([Q0])});
            skLineSegment(sketch, "E89", {"start": v(-6654.8, -2667) * mm, "end": v(-6654.8, -2743.2) * mm, "construction": true});
            skLineSegment(sketch, "E90.bottom", {"start": v(-6654.8, -2743.2) * mm, "end": v(-3809.82, -2743.2) * mm});
            skLineSegment(sketch, "E90.top", {"start": v(-6654.8, -2209.8) * mm, "end": v(-3809.82, -2209.8) * mm});
            skLineSegment(sketch, "E90.left", {"start": v(-6654.8, -2743.2) * mm, "end": v(-6654.8, -2209.8) * mm});
            skLineSegment(sketch, "E90.right", {"start": v(-3809.82, -2743.2) * mm, "end": v(-3809.82, -2209.8) * mm});
            skSolve(sketch);
        }
        {
            var Q0;
            {var subQ0=sQuery(id+"F34.wireOp",EDGE,"E90.top");Q0=makeQuery(id+"F34.imprint","IMPRINT",FACE,{"disambiguationData":[TD([[makeQuery(id+"F34.imprint","IMPRINT",EDGE,{"derivedFrom":subQ0}),-1.0]])]});}
            var Q1;
            {var subQ0=sQuery(id+"F34.wireOp",EDGE,"E90.bottom");Q1=makeQuery(id+"F34.imprint","IMPRINT",FACE,{"disambiguationData":[TD([[makeQuery(id+"F34.imprint","IMPRINT",EDGE,{"derivedFrom":subQ0}),1.0]])]});}
            extrude(context, id + "F35", {"entities" : qUnion([Q0, Q1]), "depth" : 31.75 * mm, "offsetDistance" : 25.4 * mm});
        }
        {
            var Q0;
            Q0=makeQuery(id+"F35.opExtrude","CAP_EDGE",EDGE,{"disambiguationData":[OSD([sQuery(id+"F34.wireOp",EDGE,"E90.bottom")])],"isStart":false});
            var Q1;
            Q1=makeQuery(id+"F35.opExtrude","CAP_EDGE",EDGE,{"disambiguationData":[OSD([sQuery(id+"F34.wireOp",EDGE,"E90.right")])],"isStart":false});
            var Q2;
            Q2=makeQuery(id+"F35.opExtrude","CAP_EDGE",EDGE,{"disambiguationData":[OSD([sQuery(id+"F34.wireOp",EDGE,"E90.top")])],"isStart":false});
            chamfer(context, id + "F36", {"entities" : qUnion([Q0, Q1, Q2]), "width" : 12.7 * mm, "tangentPropagation" : true});
        }
        {
            var Q0;
            Q0=makeQuery(id+"F33.opBoolean","SPLIT",FACE,{"disambiguationData":[TD([makeQuery(id+"F25.boolean.opBoolean","COPY",FACE,{"derivedFrom":makeQuery(id+"F25.opExtrude","SWEPT_FACE",FACE,{"disambiguationData":[OSD([sQuery(id+"F24.wireOp",EDGE,"E85.top")])]})})])],"derivedFrom":makeQuery(id+"F32.opExtrude","SWEPT_FACE",FACE,{"disambiguationData":[OSD([sQuery(id+"F31.wireOp",EDGE,"E88.right")])]})});
            extrude(context, id + "F37", {"entities" : qUnion([Q0]), "operationType" : NewBodyOperationType.REMOVE, "oppositeDirection" : true, "depth" : 152.4 * mm, "offsetDistance" : 25.4 * mm});
        }
        {
            var Q0;
            Q0=makeQuery(id+"F28.imprint","IMPRINT",FACE,{"disambiguationData":[TD([[makeQuery(id+"F28.imprint","IMPRINT",EDGE,{"derivedFrom":makeQuery(id+"F16.imprint","IMPRINT",EDGE,{"derivedFrom":sQuery(id+"F16.wireOp",EDGE,"E62.bottom")})}),-1.0]])]});
            var sketch = newSketch(context, id + "F38", { "sketchPlane" : qUnion([Q0])});
            skLineSegment(sketch, "E91.bottom", {"start": v(10915.14, -4793.68) * mm, "end": v(11753.34, -4793.68) * mm});
            skLineSegment(sketch, "E91.left", {"start": v(10915.14, -4793.68) * mm, "end": v(10915.14, -1593.28) * mm});
            skLineSegment(sketch, "E91.right", {"start": v(11753.34, -4793.68) * mm, "end": v(11753.34, -2431.48) * mm});
            skLineSegment(sketch, "E92.bottom", {"start": v(10915.14, -1593.28) * mm, "end": v(14725.14, -1593.28) * mm});
            skLineSegment(sketch, "E92.top", {"start": v(11753.34, -2431.48) * mm, "end": v(14725.14, -2431.48) * mm});
            skLineSegment(sketch, "E92.right", {"start": v(14725.14, -1593.28) * mm, "end": v(14725.14, -2431.48) * mm});
            skSolve(sketch);
        }
        {
            var Q0;
            Q0=makeQuery(id+"F38.imprint","IMPRINT",FACE,{"disambiguationData":[TD([[makeQuery(id+"F38.imprint","IMPRINT",EDGE,{"derivedFrom":sQuery(id+"F38.wireOp",EDGE,"E91.bottom")}),1.0]])]});
            extrude(context, id + "F39", {"entities" : qUnion([Q0]), "depth" : 914.4 * mm, "offsetDistance" : 25.4 * mm});
        }
        {
            var Q0;
            Q0=makeQuery(id+"F39.opExtrude","CAP_FACE",FACE,{"disambiguationData":[OSD([sQuery(id+"F38.wireOp",EDGE,"E91.bottom"),sQuery(id+"F38.wireOp",EDGE,"E91.left"),sQuery(id+"F38.wireOp",EDGE,"E91.right"),sQuery(id+"F38.wireOp",EDGE,"E92.bottom"),sQuery(id+"F38.wireOp",EDGE,"E92.top"),sQuery(id+"F38.wireOp",EDGE,"E92.right")])],"isStart":false});
            var sketch = newSketch(context, id + "F40", { "sketchPlane" : qUnion([Q0])});
            skLineSegment(sketch, "E93", {"start": v(11296.14, -4793.68) * mm, "end": v(11296.14, -1974.28) * mm});
            skLineSegment(sketch, "E94", {"start": v(11296.14, -1974.28) * mm, "end": v(14725.14, -1974.28) * mm});
            skLineSegment(sketch, "E95", {"start": v(14725.14, -1974.28) * mm, "end": v(14725.14, -2431.48) * mm});
            skLineSegment(sketch, "E96", {"start": v(14725.14, -2431.48) * mm, "end": v(11753.34, -2431.48) * mm});
            skLineSegment(sketch, "E97", {"start": v(11753.34, -2431.48) * mm, "end": v(11753.34, -4793.68) * mm});
            skLineSegment(sketch, "E98", {"start": v(11753.34, -4793.68) * mm, "end": v(11296.14, -4793.68) * mm});
            skSolve(sketch);
        }
        {
            var Q0;
            Q0=makeQuery(id+"F40.imprint","IMPRINT",FACE,{"disambiguationData":[TD([[makeQuery(id+"F40.imprint","IMPRINT",EDGE,{"derivedFrom":sQuery(id+"F40.wireOp",EDGE,"E93")}),-1.0]])]});
            extrude(context, id + "F41", {"entities" : qUnion([Q0]), "operationType" : NewBodyOperationType.REMOVE, "oppositeDirection" : true, "depth" : 431.8 * mm, "offsetDistance" : 25.4 * mm});
        }
        {
            var Q0;
            Q0=makeQuery(id+"F28.imprint","IMPRINT",FACE,{"disambiguationData":[TD([[makeQuery(id+"F28.imprint","IMPRINT",EDGE,{"derivedFrom":makeQuery(id+"F16.imprint","IMPRINT",EDGE,{"derivedFrom":sQuery(id+"F16.wireOp",EDGE,"E62.bottom")})}),-1.0]])]});
            var sketch = newSketch(context, id + "F42", { "sketchPlane" : qUnion([Q0])});
            skLineSegment(sketch, "E99.bottom", {"start": v(13229.39, -6380.77) * mm, "end": v(15972.59, -6380.77) * mm});
            skLineSegment(sketch, "E99.top", {"start": v(13229.39, -6990.37) * mm, "end": v(15972.59, -6990.37) * mm});
            skLineSegment(sketch, "E99.left", {"start": v(13229.39, -6380.77) * mm, "end": v(13229.39, -6990.37) * mm});
            skLineSegment(sketch, "E99.right", {"start": v(15972.59, -6380.77) * mm, "end": v(15972.59, -6990.37) * mm});
            skSolve(sketch);
        }
        {
            var Q0;
            Q0=makeQuery(id+"F42.imprint","IMPRINT",FACE,{"disambiguationData":[TD([[makeQuery(id+"F42.imprint","IMPRINT",EDGE,{"derivedFrom":sQuery(id+"F42.wireOp",EDGE,"E99.bottom")}),-1.0]])]});
            extrude(context, id + "F43", {"entities" : qUnion([Q0]), "depth" : 812.8 * mm, "offsetDistance" : 25.4 * mm});
        }
        {
            var Q0;
            Q0=makeQuery(id+"F43.opExtrude","SWEPT_FACE",FACE,{"disambiguationData":[OSD([sQuery(id+"F42.wireOp",EDGE,"E99.top")])]});
            var sketch = newSketch(context, id + "F44", { "sketchPlane" : qUnion([Q0])});
            skLineSegment(sketch, "E100.bottom", {"start": v(13229.39, 0) * mm, "end": v(13838.99, 0) * mm});
            skLineSegment(sketch, "E100.top", {"start": v(13229.39, 609.6) * mm, "end": v(13838.99, 609.6) * mm});
            skLineSegment(sketch, "E100.left", {"start": v(13229.39, 0) * mm, "end": v(13229.39, 609.6) * mm});
            skLineSegment(sketch, "E100.right", {"start": v(13838.99, 0) * mm, "end": v(13838.99, 609.6) * mm});
            skLineSegment(sketch, "E101.bottom", {"start": v(15972.59, 0) * mm, "end": v(15362.99, 0) * mm});
            skLineSegment(sketch, "E101.top", {"start": v(15972.59, 609.6) * mm, "end": v(15362.99, 609.6) * mm});
            skLineSegment(sketch, "E101.left", {"start": v(15972.59, 0) * mm, "end": v(15972.59, 609.6) * mm});
            skLineSegment(sketch, "E101.right", {"start": v(15362.99, 0) * mm, "end": v(15362.99, 609.6) * mm});
            skLineSegment(sketch, "E102.bottom", {"start": v(14042.19, 0) * mm, "end": v(15159.79, 0) * mm});
            skLineSegment(sketch, "E102.top", {"start": v(14042.19, 609.6) * mm, "end": v(15159.79, 609.6) * mm});
            skLineSegment(sketch, "E102.left", {"start": v(14042.19, 0) * mm, "end": v(14042.19, 609.6) * mm});
            skLineSegment(sketch, "E102.right", {"start": v(15159.79, 0) * mm, "end": v(15159.79, 609.6) * mm});
            skSolve(sketch);
        }
        {
            var Q0;
            Q0=makeQuery(id+"F44.imprint","IMPRINT",FACE,{"disambiguationData":[TD([[makeQuery(id+"F44.imprint","IMPRINT",EDGE,{"derivedFrom":sQuery(id+"F44.wireOp",EDGE,"E100.bottom")}),1.0]])]});
            var Q1;
            Q1=makeQuery(id+"F44.imprint","IMPRINT",FACE,{"disambiguationData":[TD([[makeQuery(id+"F44.imprint","IMPRINT",EDGE,{"derivedFrom":sQuery(id+"F44.wireOp",EDGE,"E102.bottom")}),1.0]])]});
            var Q2;
            Q2=makeQuery(id+"F44.imprint","IMPRINT",FACE,{"disambiguationData":[TD([[makeQuery(id+"F44.imprint","IMPRINT",EDGE,{"derivedFrom":sQuery(id+"F44.wireOp",EDGE,"E101.bottom")}),1.0]])]});
            extrude(context, id + "F45", {"entities" : qUnion([Q0, Q1, Q2]), "operationType" : NewBodyOperationType.REMOVE, "oppositeDirection" : true, "depth" : 609.6 * mm, "offsetDistance" : 25.4 * mm});
        }
        {
            var Q0;
            Q0=makeQuery(id+"F43.opExtrude","SWEPT_EDGE",EDGE,{"disambiguationData":[OSD([sQuery(id+"F42.wireOp",EDGE,"E99.top"),sQuery(id+"F42.wireOp",EDGE,"E99.right")])]});
            var Q1;
            Q1=makeQuery(id+"F43.opExtrude","SWEPT_EDGE",EDGE,{"disambiguationData":[OSD([sQuery(id+"F42.wireOp",EDGE,"E99.top"),sQuery(id+"F42.wireOp",EDGE,"E99.left")])]});
            var Q2;
            Q2=makeQuery(id+"F43.opExtrude","SWEPT_EDGE",EDGE,{"disambiguationData":[OSD([sQuery(id+"F42.wireOp",EDGE,"E99.bottom"),sQuery(id+"F42.wireOp",EDGE,"E99.left")])]});
            var Q3;
            Q3=makeQuery(id+"F43.opExtrude","SWEPT_EDGE",EDGE,{"disambiguationData":[OSD([sQuery(id+"F42.wireOp",EDGE,"E99.bottom"),sQuery(id+"F42.wireOp",EDGE,"E99.right")])]});
            fillet(context, id + "F46", {"entities" : qUnion([Q0, Q1, Q2, Q3]), "radius" : 127 * mm, "tangentPropagation" : true, "allowEdgeOverflow" : false});
        }
        {
            var Q0;
            Q0=makeQuery(id+"F28.imprint","IMPRINT",FACE,{"disambiguationData":[TD([[makeQuery(id+"F28.imprint","IMPRINT",EDGE,{"derivedFrom":makeQuery(id+"F16.imprint","IMPRINT",EDGE,{"derivedFrom":sQuery(id+"F16.wireOp",EDGE,"E62.bottom")})}),-1.0]])]});
            var sketch = newSketch(context, id + "F47", { "sketchPlane" : qUnion([Q0])});
            skLineSegment(sketch, "E103.bottom", {"start": v(21015.99, -1961.27) * mm, "end": v(22997.19, -1961.27) * mm});
            skLineSegment(sketch, "E103.top", {"start": v(21015.99, -2418.47) * mm, "end": v(22997.19, -2418.47) * mm});
            skLineSegment(sketch, "E103.left", {"start": v(21015.99, -1961.27) * mm, "end": v(21015.99, -2418.47) * mm});
            skLineSegment(sketch, "E103.right", {"start": v(22997.19, -1961.27) * mm, "end": v(22997.19, -2418.47) * mm});
            skSolve(sketch);
        }
        {
            var Q0;
            Q0=makeQuery(id+"F47.imprint","IMPRINT",FACE,{"disambiguationData":[TD([[makeQuery(id+"F47.imprint","IMPRINT",EDGE,{"derivedFrom":sQuery(id+"F47.wireOp",EDGE,"E103.bottom")}),-1.0]])]});
            extrude(context, id + "F48", {"entities" : qUnion([Q0]), "depth" : 1066.8 * mm, "offsetDistance" : 25.4 * mm});
        }
        {
            var Q0;
            Q0=makeQuery(id+"F48.opExtrude","SWEPT_FACE",FACE,{"disambiguationData":[OSD([sQuery(id+"F47.wireOp",EDGE,"E103.left")])]});
            extrude(context, id + "F49", {"entities" : qUnion([Q0]), "operationType" : NewBodyOperationType.ADD, "depth" : 25.4 * mm, "offsetDistance" : 25.4 * mm});
        }
        {
            var Q0;
            Q0=makeQuery(id+"F49.opExtrude","CAP_FACE",FACE,{"disambiguationData":[OSD([sQuery(id+"F47.wireOp",EDGE,"E103.left")])],"isStart":false});
            var sketch = newSketch(context, id + "F50", { "sketchPlane" : qUnion([Q0])});
            skLineSegment(sketch, "E104", {"start": v(2080.13, 1066.8) * mm, "end": v(2418.47, 909.03) * mm});
            skLineSegment(sketch, "E105.bottom", {"start": v(1999.37, 774.7) * mm, "end": v(2380.37, 774.7) * mm});
            skLineSegment(sketch, "E105.top", {"start": v(1999.37, 114.3) * mm, "end": v(2380.37, 114.3) * mm});
            skLineSegment(sketch, "E105.left", {"start": v(1999.37, 774.7) * mm, "end": v(1999.37, 114.3) * mm});
            skLineSegment(sketch, "E105.right", {"start": v(2380.37, 774.7) * mm, "end": v(2380.37, 114.3) * mm});
            skLineSegment(sketch, "E106.bottom", {"start": v(1999.37, 76.2) * mm, "end": v(2380.37, 76.2) * mm});
            skLineSegment(sketch, "E106.top", {"start": v(1999.37, 0) * mm, "end": v(2380.37, 0) * mm});
            skLineSegment(sketch, "E106.left", {"start": v(1999.37, 76.2) * mm, "end": v(1999.37, 0) * mm});
            skLineSegment(sketch, "E106.right", {"start": v(2380.37, 76.2) * mm, "end": v(2380.37, 0) * mm});
            skLineSegment(sketch, "E107", {"start": v(2418.47, 909.03) * mm, "end": v(1961.27, 909.03) * mm, "construction": true});
            skLineSegment(sketch, "E108.bottom", {"start": v(1961.27, 909.03) * mm, "end": v(2019.36, 909.03) * mm});
            skLineSegment(sketch, "E108.top", {"start": v(1961.27, 1066.8) * mm, "end": v(2019.36, 1066.8) * mm});
            skLineSegment(sketch, "E108.left", {"start": v(1961.27, 909.03) * mm, "end": v(1961.27, 1066.8) * mm});
            skLineSegment(sketch, "E108.right", {"start": v(2019.36, 909.03) * mm, "end": v(2019.36, 1066.8) * mm});
            skSolve(sketch);
        }
        {
            var Q0;
            {var subQ0=sQuery(id+"F50.wireOp",EDGE,"E104");Q0=makeQuery(id+"F50.imprint","IMPRINT",FACE,{"disambiguationData":[TD([[makeQuery(id+"F50.imprint","IMPRINT",EDGE,{"derivedFrom":subQ0}),1.0]])]});}
            var Q1;
            Q1=makeQuery(id+"F50.imprint","IMPRINT",FACE,{"disambiguationData":[TD([[makeQuery(id+"F50.imprint","IMPRINT",EDGE,{"derivedFrom":sQuery(id+"F50.wireOp",EDGE,"E108.bottom")}),1.0]])]});
            var Q2;
            Q2=makeQuery(id+"F50.imprint","IMPRINT",FACE,{"disambiguationData":[TD([[makeQuery(id+"F50.imprint","IMPRINT",EDGE,{"derivedFrom":sQuery(id+"F50.wireOp",EDGE,"E105.bottom")}),-1.0]])]});
            var Q3;
            Q3=makeQuery(id+"F50.imprint","IMPRINT",FACE,{"disambiguationData":[TD([[makeQuery(id+"F50.imprint","IMPRINT",EDGE,{"derivedFrom":sQuery(id+"F50.wireOp",EDGE,"E106.bottom")}),-1.0]])]});
            extrude(context, id + "F51", {"entities" : qUnion([Q0, Q1, Q2, Q3]), "operationType" : NewBodyOperationType.REMOVE, "endBound" : BoundingType.THROUGH_ALL, "oppositeDirection" : true, "depth" : 25.4 * mm, "offsetDistance" : 25.4 * mm});
        }
        {
            var Q0;
            {var subQ0=sQuery(id+"F47.wireOp",EDGE,"E103.top");Q0=makeQuery(id+"F49.boolean.opBoolean","MERGE",FACE,{"derivedFrom":[makeQuery(id+"F48.opExtrude","SWEPT_FACE",FACE,{"disambiguationData":[OSD([subQ0])]}),makeQuery(id+"F49.opExtrude","SWEPT_FACE",FACE,{"disambiguationData":[OSD([subQ0,sQuery(id+"F47.wireOp",EDGE,"E103.left")])]})]});}
            var sketch = newSketch(context, id + "F52", { "sketchPlane" : qUnion([Q0])});
            skLineSegment(sketch, "E109.bottom", {"start": v(21028.69, 0) * mm, "end": v(22959.09, 0) * mm});
            skLineSegment(sketch, "E109.top", {"start": v(21028.69, 76.2) * mm, "end": v(22959.09, 76.2) * mm});
            skLineSegment(sketch, "E109.left", {"start": v(21028.69, 0) * mm, "end": v(21028.69, 76.2) * mm});
            skLineSegment(sketch, "E109.right", {"start": v(22959.09, 0) * mm, "end": v(22959.09, 76.2) * mm});
            skLineSegment(sketch, "E110.bottom", {"start": v(21028.69, 114.3) * mm, "end": v(22959.09, 114.3) * mm});
            skLineSegment(sketch, "E110.top", {"start": v(21028.69, 774.7) * mm, "end": v(22959.09, 774.7) * mm});
            skLineSegment(sketch, "E110.left", {"start": v(21028.69, 114.3) * mm, "end": v(21028.69, 774.7) * mm});
            skLineSegment(sketch, "E110.right", {"start": v(22959.09, 114.3) * mm, "end": v(22959.09, 774.7) * mm});
            skSolve(sketch);
        }
        {
            var Q0;
            Q0=makeQuery(id+"F52.imprint","IMPRINT",FACE,{"disambiguationData":[TD([[makeQuery(id+"F52.imprint","IMPRINT",EDGE,{"derivedFrom":sQuery(id+"F52.wireOp",EDGE,"E110.bottom")}),1.0]])]});
            var Q1;
            Q1=makeQuery(id+"F52.imprint","IMPRINT",FACE,{"disambiguationData":[TD([[makeQuery(id+"F52.imprint","IMPRINT",EDGE,{"derivedFrom":sQuery(id+"F52.wireOp",EDGE,"E109.bottom")}),1.0]])]});
            extrude(context, id + "F53", {"entities" : qUnion([Q0, Q1]), "operationType" : NewBodyOperationType.REMOVE, "endBound" : BoundingType.THROUGH_ALL, "oppositeDirection" : true, "depth" : 25.4 * mm, "offsetDistance" : 25.4 * mm});
        }
        {
            var Q0;
            Q0=makeQuery(id+"F28.imprint","IMPRINT",FACE,{"disambiguationData":[TD([[makeQuery(id+"F28.imprint","IMPRINT",EDGE,{"derivedFrom":makeQuery(id+"F16.imprint","IMPRINT",EDGE,{"derivedFrom":sQuery(id+"F16.wireOp",EDGE,"E62.bottom")})}),-1.0]])]});
            var sketch = newSketch(context, id + "F54", { "sketchPlane" : qUnion([Q0])});
            skLineSegment(sketch, "E111.bottom", {"start": v(23594.75, -5758.56) * mm, "end": v(26033.15, -5758.56) * mm});
            skLineSegment(sketch, "E111.top", {"start": v(23594.75, -4539.36) * mm, "end": v(26033.15, -4539.36) * mm});
            skLineSegment(sketch, "E111.left", {"start": v(23594.75, -5758.56) * mm, "end": v(23594.75, -4539.36) * mm});
            skLineSegment(sketch, "E111.right", {"start": v(26033.15, -5758.56) * mm, "end": v(26033.15, -4539.36) * mm});
            skSolve(sketch);
        }
        {
            var Q0;
            Q0=makeQuery(id+"F54.imprint","IMPRINT",FACE,{"disambiguationData":[TD([[makeQuery(id+"F54.imprint","IMPRINT",EDGE,{"derivedFrom":sQuery(id+"F54.wireOp",EDGE,"E111.bottom")}),1.0]])]});
            extrude(context, id + "F55", {"entities" : qUnion([Q0]), "depth" : 2235.2 * mm, "offsetDistance" : 25.4 * mm});
        }
        {
            var Q0;
            Q0=makeQuery(id+"F55.opExtrude","SWEPT_FACE",FACE,{"disambiguationData":[OSD([sQuery(id+"F54.wireOp",EDGE,"E111.bottom")])]});
            var sketch = newSketch(context, id + "F56", { "sketchPlane" : qUnion([Q0])});
            skLineSegment(sketch, "E112", {"start": v(23594.75, 1016) * mm, "end": v(25118.75, 1770.96) * mm});
            skLineSegment(sketch, "E113", {"start": v(25118.75, 1770.96) * mm, "end": v(25118.75, 2235.2) * mm});
            skSolve(sketch);
        }
        {
            var Q0;
            Q0 = qSketchRegion(id + "F56", true);
            var Q1;
            {var subQ0=sQuery(id+"F56.wireOp",EDGE,"E112");Q1=makeQuery(id+"F56.imprint","IMPRINT",FACE,{"disambiguationData":[TD([[makeQuery(id+"F56.imprint","IMPRINT",EDGE,{"derivedFrom":subQ0}),1.0]])]});}
            extrude(context, id + "F57", {"entities" : qUnion([Q0, Q1]), "operationType" : NewBodyOperationType.REMOVE, "endBound" : BoundingType.THROUGH_ALL, "oppositeDirection" : true, "depth" : 25.4 * mm, "offsetDistance" : 25.4 * mm});
        }
        {
            var Q0;
            Q0=makeQuery(id+"F28.imprint","IMPRINT",FACE,{"disambiguationData":[TD([[makeQuery(id+"F28.imprint","IMPRINT",EDGE,{"derivedFrom":makeQuery(id+"F16.imprint","IMPRINT",EDGE,{"derivedFrom":sQuery(id+"F16.wireOp",EDGE,"E62.bottom")})}),-1.0]])]});
            var sketch = newSketch(context, id + "F58", { "sketchPlane" : qUnion([Q0])});
            skLineSegment(sketch, "E114.bottom", {"start": v(18028.59, -9466.35) * mm, "end": v(19171.59, -9466.35) * mm});
            skLineSegment(sketch, "E114.top", {"start": v(18028.59, -8628.15) * mm, "end": v(19171.59, -8628.15) * mm});
            skLineSegment(sketch, "E114.left", {"start": v(18028.59, -9466.35) * mm, "end": v(18028.59, -8628.15) * mm});
            skLineSegment(sketch, "E114.right", {"start": v(19171.59, -9466.35) * mm, "end": v(19171.59, -8628.15) * mm});
            skSolve(sketch);
        }
        {
            var Q0;
            Q0=makeQuery(id+"F58.imprint","IMPRINT",FACE,{"disambiguationData":[TD([[makeQuery(id+"F58.imprint","IMPRINT",EDGE,{"derivedFrom":sQuery(id+"F58.wireOp",EDGE,"E114.bottom")}),1.0]])]});
            extrude(context, id + "F59", {"entities" : qUnion([Q0]), "depth" : 965.2 * mm, "offsetDistance" : 25.4 * mm});
        }
        {
            var Q0;
            Q0=makeQuery(id+"F28.imprint","IMPRINT",FACE,{"disambiguationData":[TD([[makeQuery(id+"F28.imprint","IMPRINT",EDGE,{"derivedFrom":makeQuery(id+"F16.imprint","IMPRINT",EDGE,{"derivedFrom":sQuery(id+"F16.wireOp",EDGE,"E62.bottom")})}),-1.0]])]});
            var sketch = newSketch(context, id + "F60", { "sketchPlane" : qUnion([Q0])});
            skLineSegment(sketch, "E115.bottom", {"start": v(22903.18, -10690.11) * mm, "end": v(24122.38, -10690.11) * mm});
            skLineSegment(sketch, "E115.top", {"start": v(22903.18, -10080.51) * mm, "end": v(24122.38, -10080.51) * mm});
            skLineSegment(sketch, "E115.left", {"start": v(22903.18, -10690.11) * mm, "end": v(22903.18, -10080.51) * mm});
            skLineSegment(sketch, "E115.right", {"start": v(24122.38, -10690.11) * mm, "end": v(24122.38, -10080.51) * mm});
            skSolve(sketch);
        }
        {
            var Q0;
            Q0=makeQuery(id+"F60.imprint","IMPRINT",FACE,{"disambiguationData":[TD([[makeQuery(id+"F60.imprint","IMPRINT",EDGE,{"derivedFrom":sQuery(id+"F60.wireOp",EDGE,"E115.bottom")}),1.0]])]});
            extrude(context, id + "F61", {"entities" : qUnion([Q0]), "depth" : 838.2 * mm, "offsetDistance" : 25.4 * mm});
        }
        {
            var Q0;
            Q0=makeQuery(id+"F61.opExtrude","CAP_EDGE",EDGE,{"disambiguationData":[OSD([sQuery(id+"F60.wireOp",EDGE,"E115.left")])],"isStart":false});
            var Q1;
            Q1=makeQuery(id+"F61.opExtrude","CAP_EDGE",EDGE,{"disambiguationData":[OSD([sQuery(id+"F60.wireOp",EDGE,"E115.right")])],"isStart":false});
            chamfer(context, id + "F62", {"entities" : qUnion([Q0, Q1]), "width" : 127 * mm, "tangentPropagation" : true});
        }
        {
            var Q0;
            Q0=makeQuery(id+"F61.opExtrude","SWEPT_FACE",FACE,{"disambiguationData":[OSD([sQuery(id+"F60.wireOp",EDGE,"E115.bottom")])]});
            var sketch = newSketch(context, id + "F63", { "sketchPlane" : qUnion([Q0])});
            skLineSegment(sketch, "E116.bottom", {"start": v(23072.4, 0) * mm, "end": v(23941.22, 0) * mm});
            skLineSegment(sketch, "E116.top", {"start": v(23072.4, 535.8) * mm, "end": v(23941.22, 535.8) * mm});
            skLineSegment(sketch, "E116.left", {"start": v(23072.4, 0) * mm, "end": v(23072.4, 535.8) * mm});
            skLineSegment(sketch, "E116.right", {"start": v(23941.22, 0) * mm, "end": v(23941.22, 535.8) * mm});
            skSolve(sketch);
        }
        {
            var Q0;
            Q0 = qSketchRegion(id + "F63", true);
            var Q1;
            Q1=makeQuery(id+"F63.imprint","IMPRINT",FACE,{"disambiguationData":[TD([[makeQuery(id+"F63.imprint","IMPRINT",EDGE,{"derivedFrom":sQuery(id+"F63.wireOp",EDGE,"E116.bottom")}),1.0]])]});
            extrude(context, id + "F64", {"entities" : qUnion([Q0, Q1]), "operationType" : NewBodyOperationType.REMOVE, "oppositeDirection" : true, "depth" : 609.6 * mm, "offsetDistance" : 25.4 * mm});
        }
        {
            var Q0;
            Q0=makeQuery(id+"F59.opExtrude","SWEPT_FACE",FACE,{"disambiguationData":[OSD([sQuery(id+"F58.wireOp",EDGE,"E114.bottom")])]});
            var sketch = newSketch(context, id + "F65", { "sketchPlane" : qUnion([Q0])});
            skLineSegment(sketch, "E117.bottom", {"start": v(18260.11, 0) * mm, "end": v(18948.95, 0) * mm});
            skLineSegment(sketch, "E117.top", {"start": v(18260.11, 509.38) * mm, "end": v(18948.95, 509.38) * mm});
            skLineSegment(sketch, "E117.left", {"start": v(18260.11, 0) * mm, "end": v(18260.11, 509.38) * mm});
            skLineSegment(sketch, "E117.right", {"start": v(18948.95, 0) * mm, "end": v(18948.95, 509.38) * mm});
            skSolve(sketch);
        }
        {
            var Q0;
            Q0=makeQuery(id+"F65.imprint","IMPRINT",FACE,{"disambiguationData":[TD([[makeQuery(id+"F65.imprint","IMPRINT",EDGE,{"derivedFrom":sQuery(id+"F65.wireOp",EDGE,"E117.bottom")}),1.0]])]});
            extrude(context, id + "F66", {"entities" : qUnion([Q0]), "operationType" : NewBodyOperationType.REMOVE, "oppositeDirection" : true, "depth" : 838.2 * mm, "offsetDistance" : 25.4 * mm});
        }
        {
            var Q0;
            Q0=makeQuery(id+"F59.opExtrude","SWEPT_FACE",FACE,{"disambiguationData":[OSD([sQuery(id+"F58.wireOp",EDGE,"E114.left")])]});
            var sketch = newSketch(context, id + "F67", { "sketchPlane" : qUnion([Q0])});
            skPoint(sketch, "E118.oppositeSnap0", {"position": v(9466.35, 482.6) * mm});
            skLineSegment(sketch, "E118.bottom", {"start": v(8746.73, 0) * mm, "end": v(9306.5, 0) * mm});
            skLineSegment(sketch, "E118.top", {"start": v(8746.73, 482.6) * mm, "end": v(9306.5, 482.6) * mm});
            skLineSegment(sketch, "E118.left", {"start": v(8746.73, 0) * mm, "end": v(8746.73, 482.6) * mm});
            skLineSegment(sketch, "E118.right", {"start": v(9306.5, 0) * mm, "end": v(9306.5, 482.6) * mm});
            skSolve(sketch);
        }
        {
            var Q0;
            Q0 = qSketchRegion(id + "F67", true);
            extrude(context, id + "F68", {"entities" : qUnion([Q0]), "operationType" : NewBodyOperationType.REMOVE, "oppositeDirection" : true, "depth" : 1143 * mm, "offsetDistance" : 25.4 * mm});
        }
    });
